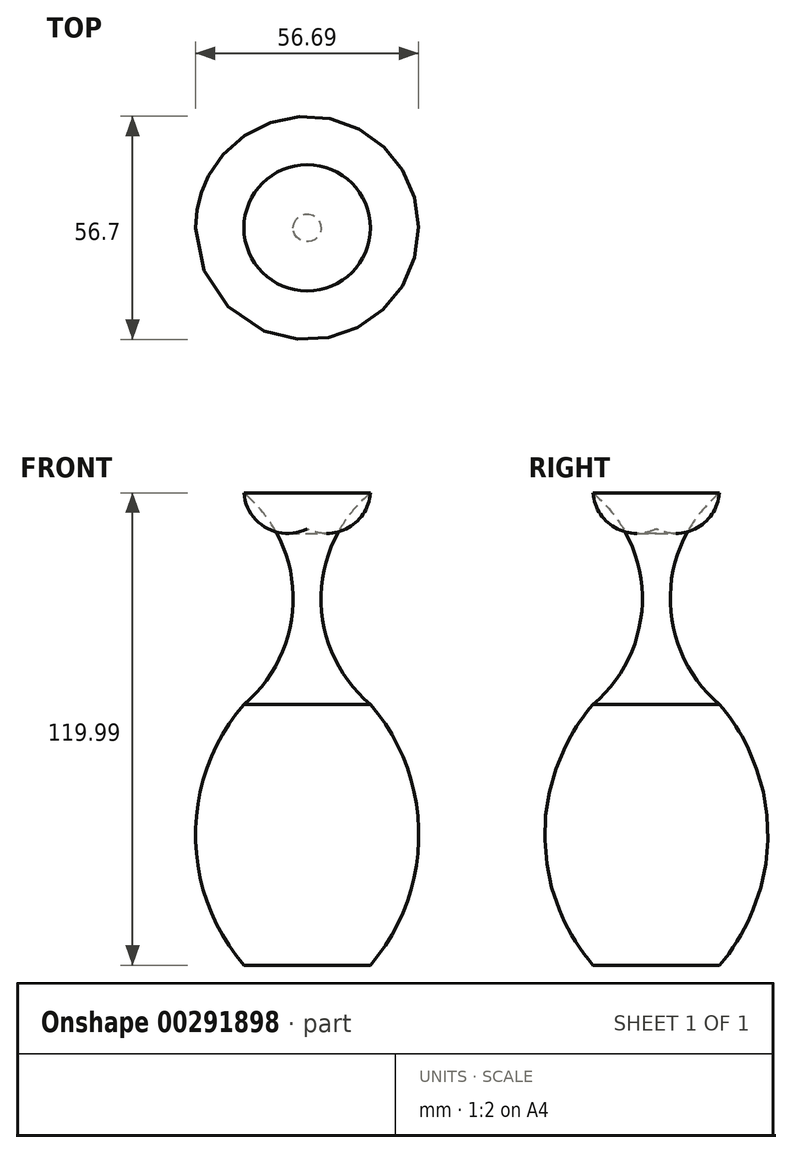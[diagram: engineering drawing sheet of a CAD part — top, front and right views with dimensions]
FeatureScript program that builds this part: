
annotation { "Feature Type Name" : "Feature", "Feature Type Description" : "" }
export const myFeature = defineFeature(function(context is Context, id is Id, definition is map)
    precondition{}
    {
        {
            var Q0;
            Q0=qCreatedBy(makeId("Front.planeOp"),FACE);
            var sketch = newSketch(context, id + "F0", { "sketchPlane" : qUnion([Q0])});
            skLineSegment(sketch, "E0", {"start": v(0.47, 0) * mm, "end": v(-15.58, 0) * mm});
            skArc(sketch, "E1", {"start": v(-15.58, 66.29) * mm, "mid": v(-27.87, 33.14) * mm, "end": v(-15.58, 0) * mm});
            skLineSegment(sketch, "E2", {"start": v(-15.58, 66.29) * mm, "end": v(-28.9, 66.29) * mm});
            skArc(sketch, "E3", {"start": v(-15.58, 66.29) * mm, "mid": v(-3.07, 93.14) * mm, "end": v(-15.58, 120) * mm});
            skLineSegment(sketch, "E4", {"start": v(0.47, 0) * mm, "end": v(0.47, 153.03) * mm});
            skLineSegment(sketch, "E5", {"start": v(0.47, 0) * mm, "end": v(0.47, 130.76) * mm});
            skArc(sketch, "E6", {"start": v(0.47, 130.76) * mm, "mid": v(-10.69, 130.04) * mm, "end": v(-15.58, 120) * mm});
            skSolve(sketch);
        }
        {
            var Q0;
            Q0=makeQuery(id+"F0.imprint","IMPRINT",FACE,{"disambiguationData":[TD([[makeQuery(id+"F0.imprint","IMPRINT",EDGE,{"derivedFrom":sQuery(id+"F0.wireOp",EDGE,"E0")}),-1.0]])]});
            var Q1;
            Q1=sQuery(id+"F0.wireOp",EDGE,"E5");
            revolve(context, id + "F1", {"entities" : qUnion([Q0]), "axis" : qUnion([Q1]), "revolveType" : RevolveType.FULL});
        }
    });
